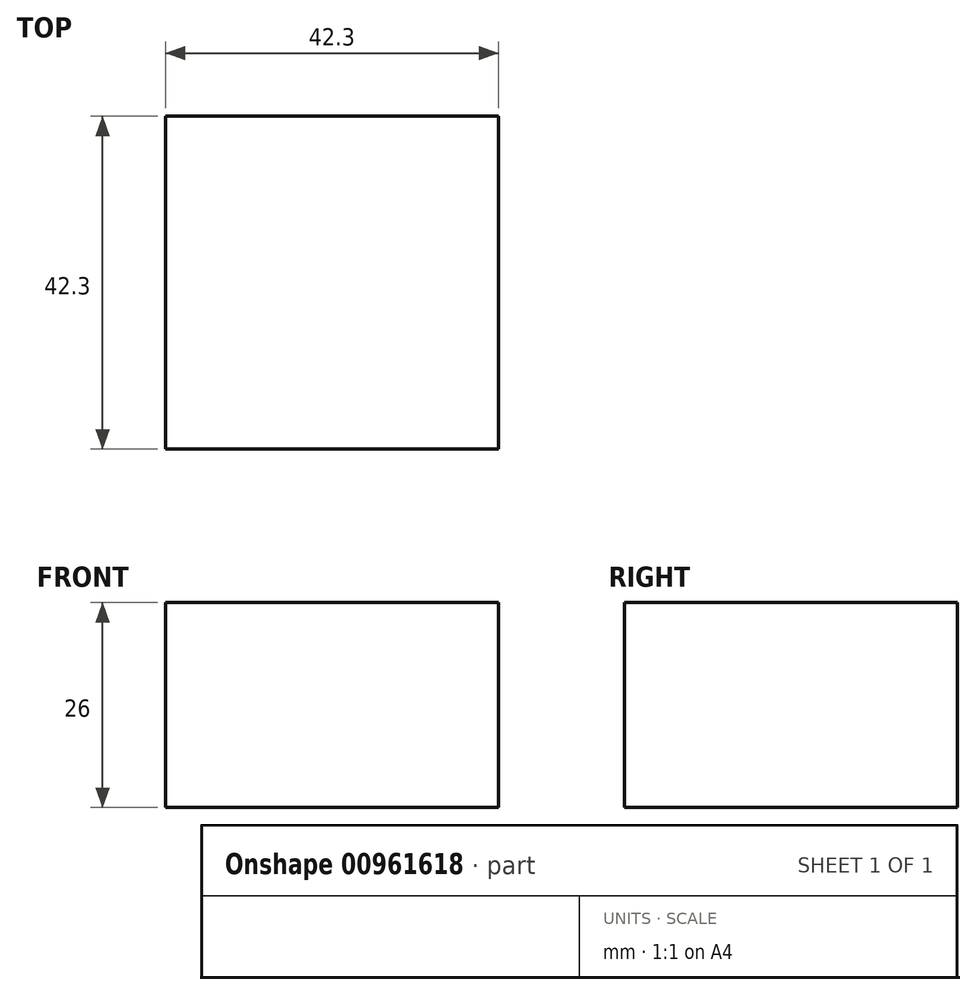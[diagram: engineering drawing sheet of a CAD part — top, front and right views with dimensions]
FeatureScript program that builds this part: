
annotation { "Feature Type Name" : "Feature", "Feature Type Description" : "" }
export const myFeature = defineFeature(function(context is Context, id is Id, definition is map)
    precondition{}
    {
        {
            var Q0;
            Q0=qCreatedBy(makeId("Top.planeOp"),FACE);
            var sketch = newSketch(context, id + "F0", { "sketchPlane" : qUnion([Q0])});
            skLineSegment(sketch, "E0.bottom", {"start": v(-37.48, 24.28) * mm, "end": v(4.82, 24.28) * mm});
            skLineSegment(sketch, "E0.top", {"start": v(-37.48, -18.02) * mm, "end": v(4.82, -18.02) * mm});
            skLineSegment(sketch, "E0.left", {"start": v(-37.48, 24.28) * mm, "end": v(-37.48, -18.02) * mm});
            skLineSegment(sketch, "E0.right", {"start": v(4.82, 24.28) * mm, "end": v(4.82, -18.02) * mm});
            skSolve(sketch);
        }
        {
            var Q0;
            Q0 = qSketchRegion(id + "F0", true);
            extrude(context, id + "F1", {"entities" : qUnion([Q0]), "depth" : 26 * mm, "offsetDistance" : 25.4 * mm});
        }
    });
